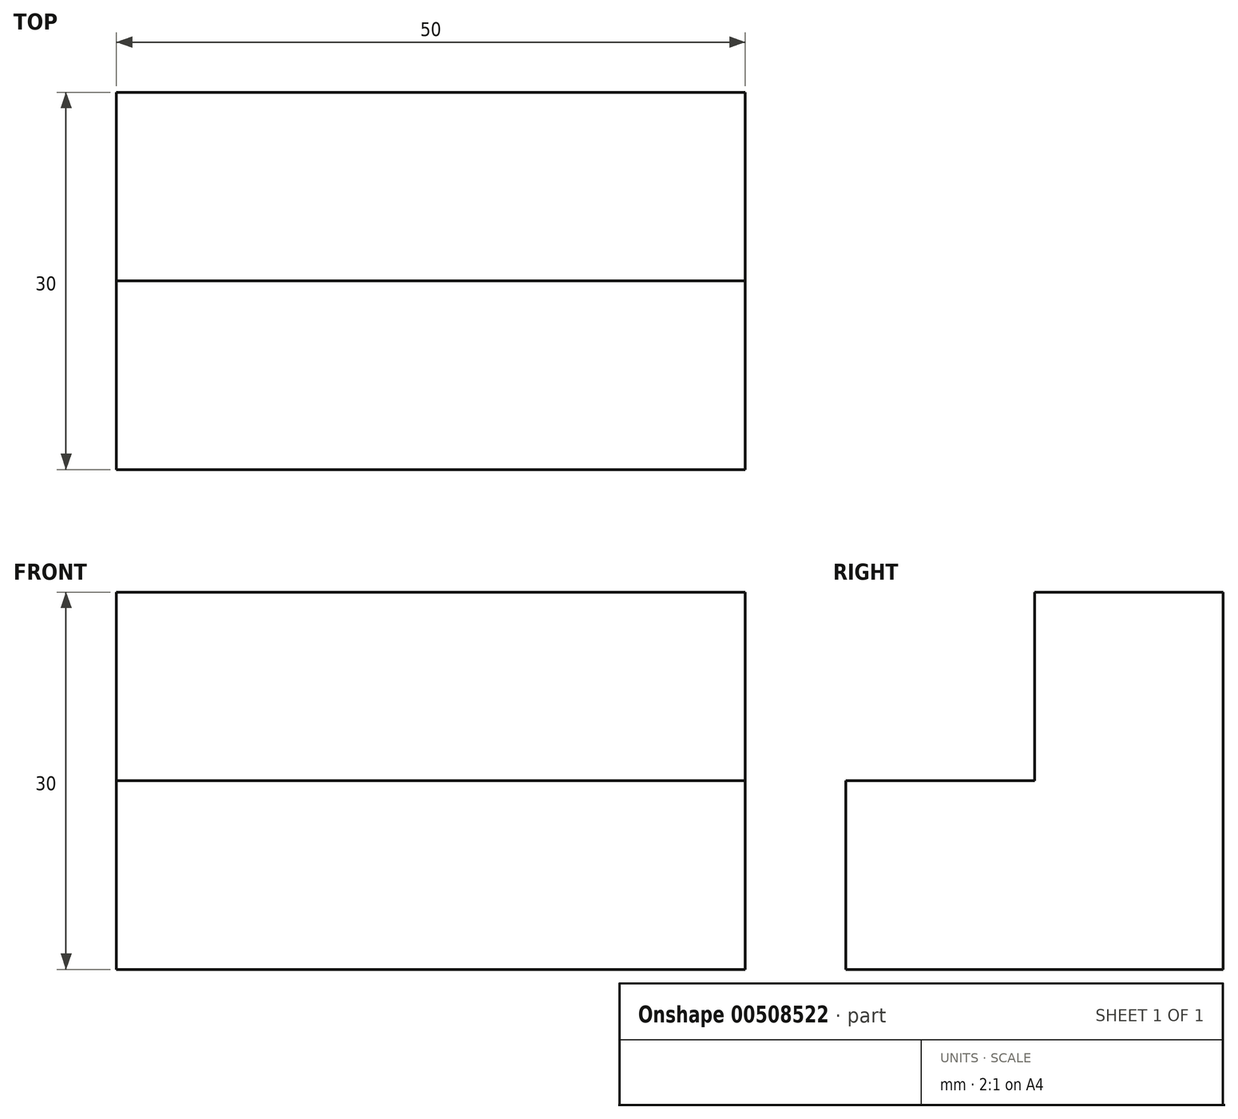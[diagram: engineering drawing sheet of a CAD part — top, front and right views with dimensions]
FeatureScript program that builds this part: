
annotation { "Feature Type Name" : "Feature", "Feature Type Description" : "" }
export const myFeature = defineFeature(function(context is Context, id is Id, definition is map)
    precondition{}
    {
        {
            var Q0;
            Q0=qCreatedBy(makeId("Front.planeOp"),FACE);
            var sketch = newSketch(context, id + "F0", { "sketchPlane" : qUnion([Q0])});
            skLineSegment(sketch, "E0", {"start": v(0, 0) * mm, "end": v(-50, 0) * mm});
            skLineSegment(sketch, "E1", {"start": v(-50, 0) * mm, "end": v(-50, 15) * mm});
            skLineSegment(sketch, "E2", {"start": v(-50, 15) * mm, "end": v(0, 15) * mm});
            skLineSegment(sketch, "E3", {"start": v(0, 15) * mm, "end": v(0, 0) * mm});
            skSolve(sketch);
        }
        {
            var Q0;
            Q0=qCreatedBy(makeId("Right.planeOp"),FACE);
            var sketch = newSketch(context, id + "F1", { "sketchPlane" : qUnion([Q0])});
            skLineSegment(sketch, "E4", {"start": v(0, 15) * mm, "end": v(15, 15) * mm});
            skLineSegment(sketch, "E5", {"start": v(15, 15) * mm, "end": v(15, 30) * mm});
            skLineSegment(sketch, "E6", {"start": v(15, 30) * mm, "end": v(30, 30) * mm});
            skLineSegment(sketch, "E7", {"start": v(30, 30) * mm, "end": v(30, 0) * mm});
            skLineSegment(sketch, "E8", {"start": v(30, 0) * mm, "end": v(0, 0) * mm});
            skLineSegment(sketch, "E9", {"start": v(0, 15) * mm, "end": v(0, 0) * mm});
            skSolve(sketch);
        }
        {
            var Q0;
            Q0=makeQuery(id+"F0.imprint","IMPRINT",FACE,{"disambiguationData":[TD([[makeQuery(id+"F0.imprint","IMPRINT",EDGE,{"derivedFrom":sQuery(id+"F0.wireOp",EDGE,"E0")}),-1.0]])]});
            extrude(context, id + "F2", {"entities" : qUnion([Q0]), "oppositeDirection" : true, "depth" : 30 * mm});
        }
        {
            var Q0;
            Q0=makeQuery(id+"F1.imprint","IMPRINT",FACE,{"disambiguationData":[TD([[makeQuery(id+"F1.imprint","IMPRINT",EDGE,{"derivedFrom":sQuery(id+"F1.wireOp",EDGE,"E4")}),-1.0]])]});
            extrude(context, id + "F3", {"entities" : qUnion([Q0]), "operationType" : NewBodyOperationType.ADD, "oppositeDirection" : true, "depth" : 50 * mm});
        }
    });
